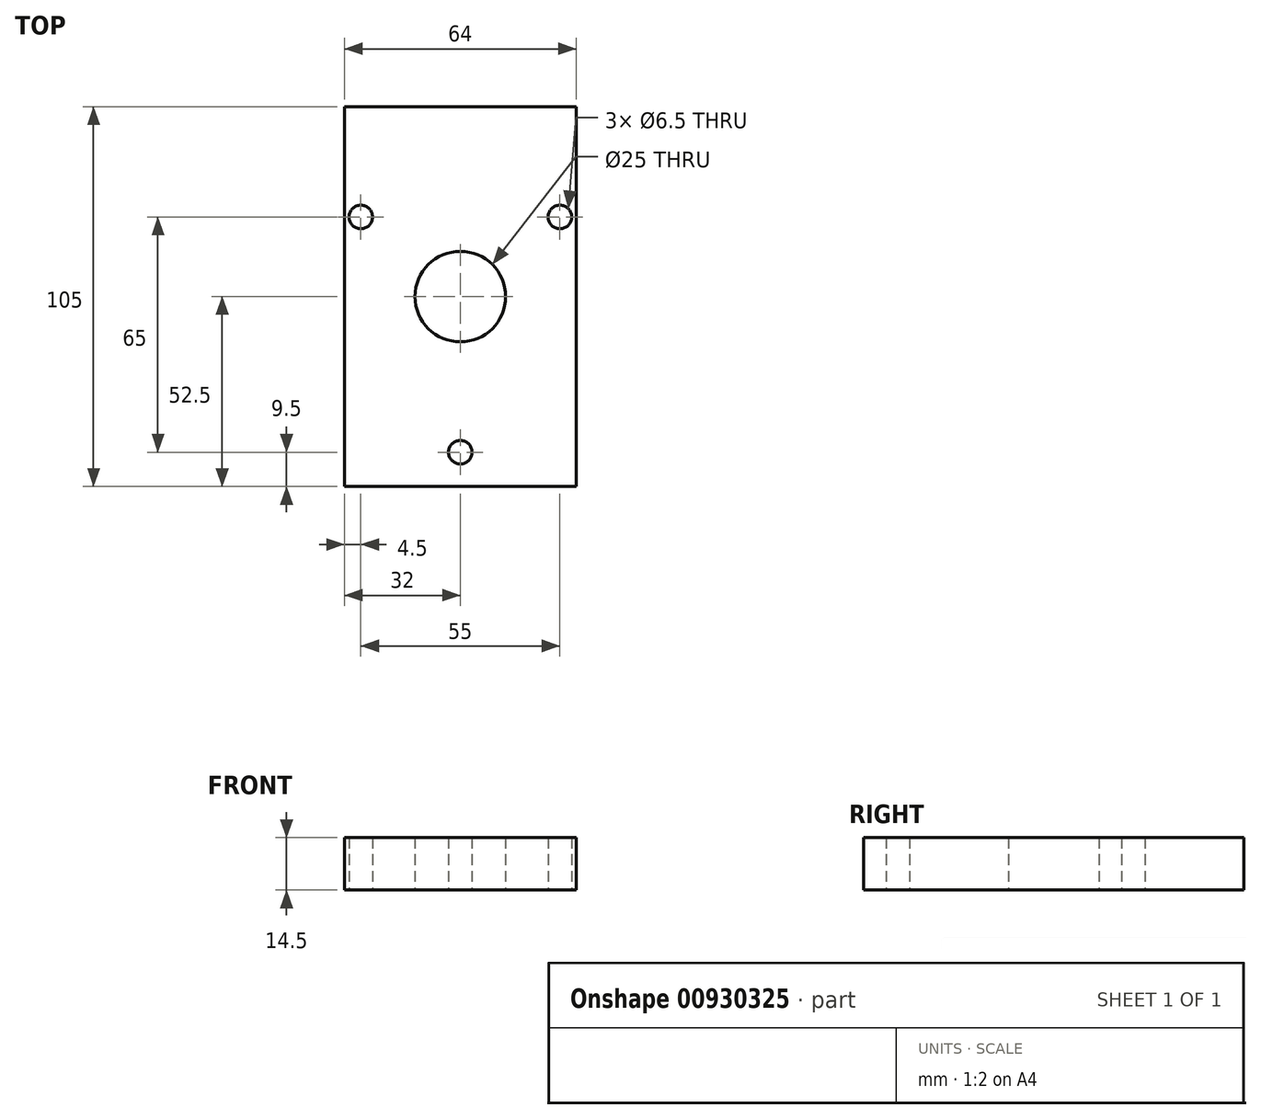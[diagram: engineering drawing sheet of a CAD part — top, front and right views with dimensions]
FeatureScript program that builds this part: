
annotation { "Feature Type Name" : "Feature", "Feature Type Description" : "" }
export const myFeature = defineFeature(function(context is Context, id is Id, definition is map)
    precondition{}
    {
        {
            var Q0;
            Q0=qCreatedBy(makeId("Top.planeOp"),FACE);
            var sketch = newSketch(context, id + "F0", { "sketchPlane" : qUnion([Q0])});
            skLineSegment(sketch, "E0", {"start": v(-27.5, 0) * mm, "end": v(27.5, 0) * mm, "construction": true});
            skPoint(sketch, "E1", {"position": v(0, 0) * mm});
            skCircle(sketch, "E2", {"center": v(-27.5, 0) * mm, "radius": 3.25 * mm});
            skCircle(sketch, "E3", {"center": v(27.5, 0) * mm, "radius": 3.25 * mm});
            skLineSegment(sketch, "E4", {"start": v(0, 0) * mm, "end": v(0, -65) * mm, "construction": true});
            skCircle(sketch, "E5", {"center": v(0, -65) * mm, "radius": 3.25 * mm});
            skLineSegment(sketch, "E6", {"start": v(-20.55, -22) * mm, "end": v(24.08, -22) * mm, "construction": true});
            skCircle(sketch, "E7", {"center": v(0, -22) * mm, "radius": 12.5 * mm});
            skLineSegment(sketch, "E8.bottom", {"start": v(32, -74.5) * mm, "end": v(-32, -74.5) * mm});
            skLineSegment(sketch, "E8.top", {"start": v(32, 30.5) * mm, "end": v(-32, 30.5) * mm});
            skLineSegment(sketch, "E8.left", {"start": v(32, -74.5) * mm, "end": v(32, 30.5) * mm});
            skLineSegment(sketch, "E8.right", {"start": v(-32, -74.5) * mm, "end": v(-32, 30.5) * mm});
            skSolve(sketch);
        }
        {
            var Q0;
            Q0=makeQuery(id+"F0.imprint","IMPRINT",FACE,{"disambiguationData":[TD([[makeQuery(id+"F0.imprint","IMPRINT",EDGE,{"derivedFrom":sQuery(id+"F0.wireOp",EDGE,"E2")}),-1.0]])]});
            extrude(context, id + "F1", {"entities" : qUnion([Q0]), "depth" : 14.5 * mm, "offsetDistance" : 25 * mm});
        }
    });
